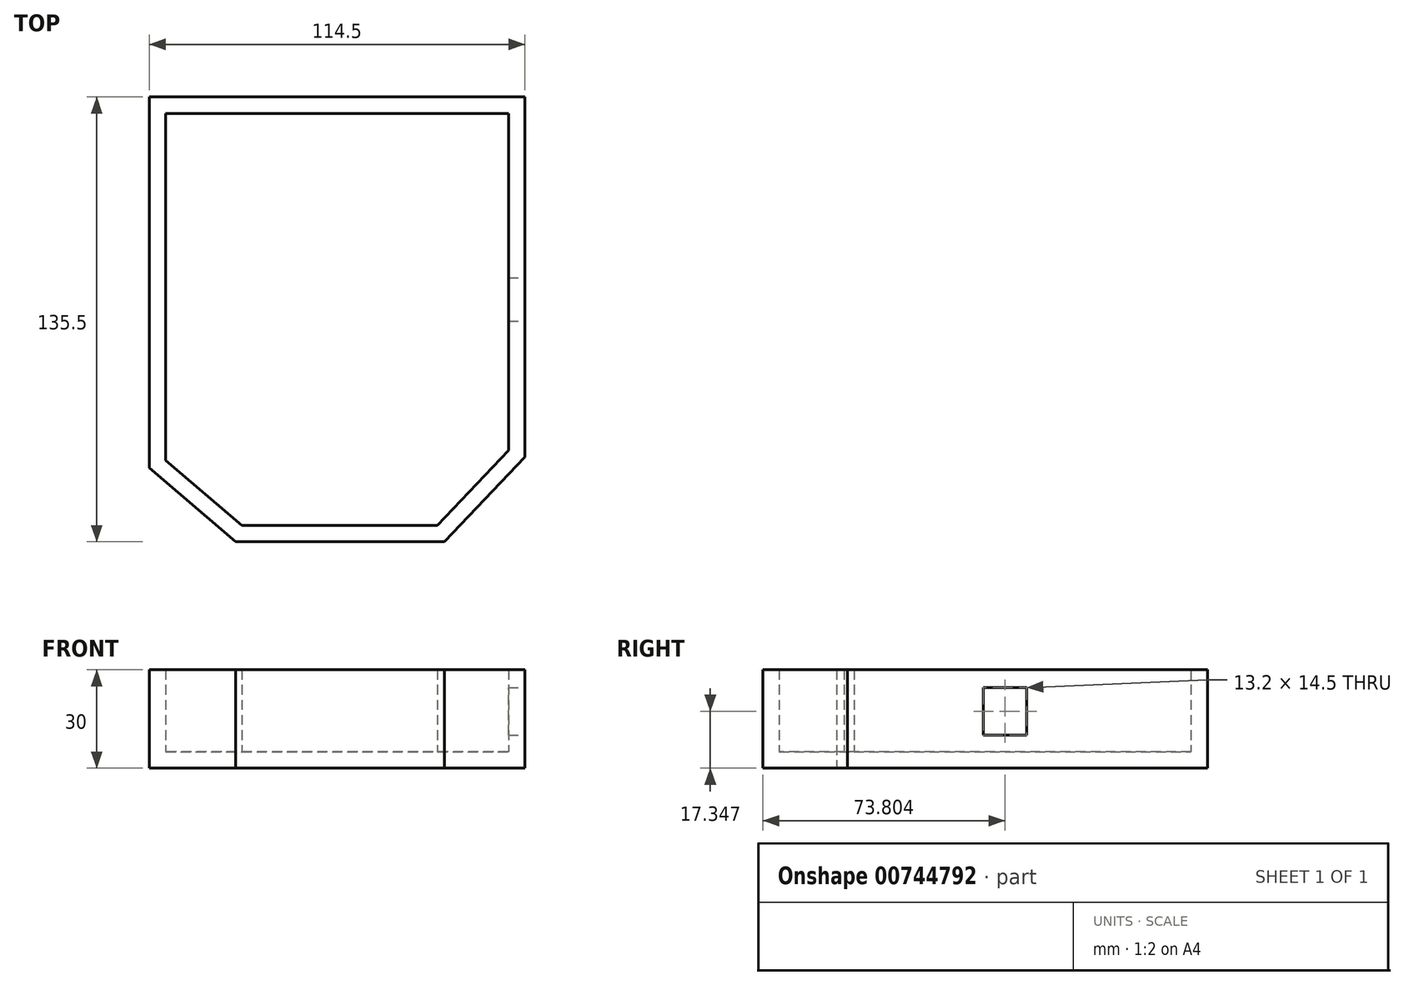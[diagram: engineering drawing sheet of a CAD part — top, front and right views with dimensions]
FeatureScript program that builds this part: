
annotation { "Feature Type Name" : "Feature", "Feature Type Description" : "" }
export const myFeature = defineFeature(function(context is Context, id is Id, definition is map)
    precondition{}
    {
        {
            var Q0;
            Q0=qCreatedBy(makeId("Top.planeOp"),FACE);
            var sketch = newSketch(context, id + "F0", { "sketchPlane" : qUnion([Q0])});
            skLineSegment(sketch, "E0.bottom", {"start": v(-53, 54.87) * mm, "end": v(61.5, 54.87) * mm});
            skLineSegment(sketch, "E0.top", {"start": v(-28.5, -80.63) * mm, "end": v(37, -80.63) * mm});
            skLineSegment(sketch, "E0.left", {"start": v(-53, 54.87) * mm, "end": v(-53, -58.13) * mm});
            skLineSegment(sketch, "E0.right", {"start": v(61.5, 54.87) * mm, "end": v(61.5, -54.87) * mm});
            skLineSegment(sketch, "E1", {"start": v(-53, -58.13) * mm, "end": v(-26.67, -80.63) * mm});
            skLineSegment(sketch, "E2", {"start": v(-28.5, -80.63) * mm, "end": v(-26.67, -80.63) * mm});
            skLineSegment(sketch, "E3", {"start": v(37, -80.63) * mm, "end": v(61.5, -54.87) * mm});
            skPoint(sketch, "E4.orphan", {"position": v(-53, -80.63) * mm});
            skPoint(sketch, "E5.orphan", {"position": v(61.5, -80.63) * mm});
            skPoint(sketch, "E6.end.orphan", {"position": v(63.33, -58.13) * mm});
            skSolve(sketch);
        }
        {
            var Q0;
            Q0 = qSketchRegion(id + "F0", true);
            extrude(context, id + "F1", {"entities" : qUnion([Q0]), "depth" : 5 * mm, "offsetDistance" : 25 * mm});
        }
        {
            var Q0;
            Q0=makeQuery(id+"F1.opExtrude","CAP_FACE",FACE,{"disambiguationData":[OSD([sQuery(id+"F0.wireOp",EDGE,"E0.bottom"),sQuery(id+"F0.wireOp",EDGE,"E0.top"),sQuery(id+"F0.wireOp",EDGE,"E0.left"),sQuery(id+"F0.wireOp",EDGE,"E0.right"),sQuery(id+"F0.wireOp",EDGE,"E1"),sQuery(id+"F0.wireOp",EDGE,"E3")])],"isStart":false});
            var sketch = newSketch(context, id + "F2", { "sketchPlane" : qUnion([Q0])});
            skLineSegment(sketch, "E7.0", {"start": v(-48, 49.87) * mm, "end": v(-48, -55.83) * mm});
            skLineSegment(sketch, "E7.1", {"start": v(-24.83, -75.63) * mm, "end": v(34.86, -75.63) * mm});
            skLineSegment(sketch, "E7.2", {"start": v(34.86, -75.63) * mm, "end": v(56.5, -52.87) * mm});
            skLineSegment(sketch, "E7.3", {"start": v(-48, -55.83) * mm, "end": v(-24.83, -75.63) * mm});
            skLineSegment(sketch, "E7.4", {"start": v(56.5, -52.87) * mm, "end": v(56.5, 49.87) * mm});
            skLineSegment(sketch, "E7.5", {"start": v(56.5, 49.87) * mm, "end": v(-48, 49.87) * mm});
            skSolve(sketch);
        }
        {
            var Q0;
            Q0=makeQuery(id+"F2.imprint","IMPRINT",FACE,{"disambiguationData":[TD([[makeQuery(id+"F2.imprint","IMPRINT",EDGE,{"derivedFrom":sQuery(id+"F2.wireOp",EDGE,"E7.0")}),-1.0]])]});
            extrude(context, id + "F3", {"entities" : qUnion([Q0]), "operationType" : NewBodyOperationType.ADD, "depth" : 25 * mm, "offsetDistance" : 25 * mm});
        }
        {
            var Q0;
            {var subQ0=sQuery(id+"F0.wireOp",EDGE,"E0.right");Q0=makeQuery(id+"F3.boolean.opBoolean","MERGE",FACE,{"derivedFrom":[makeQuery(id+"F1.opExtrude","SWEPT_FACE",FACE,{"disambiguationData":[OSD([subQ0])]}),makeQuery(id+"F3.opExtrude","SWEPT_FACE",FACE,{"disambiguationData":[OSD([subQ0])]})]});}
            var sketch = newSketch(context, id + "F4", { "sketchPlane" : qUnion([Q0])});
            skLineSegment(sketch, "E8.bottom", {"start": v(10.11, 12.6) * mm, "end": v(52.11, 12.6) * mm});
            skLineSegment(sketch, "E8.top", {"start": v(10.11, 5) * mm, "end": v(52.11, 5) * mm});
            skLineSegment(sketch, "E8.left", {"start": v(10.11, 12.6) * mm, "end": v(10.11, 5) * mm});
            skLineSegment(sketch, "E8.right", {"start": v(52.11, 12.6) * mm, "end": v(52.11, 5) * mm});
            skSolve(sketch);
        }
        {
            var Q0;
            {var subQ0=sQuery(id+"F0.wireOp",EDGE,"E0.right");Q0=makeQuery(id+"F3.boolean.opBoolean","MERGE",FACE,{"derivedFrom":[makeQuery(id+"F1.opExtrude","SWEPT_FACE",FACE,{"disambiguationData":[OSD([subQ0])]}),makeQuery(id+"F3.opExtrude","SWEPT_FACE",FACE,{"disambiguationData":[OSD([subQ0])]})]});}
            var sketch = newSketch(context, id + "F5", { "sketchPlane" : qUnion([Q0])});
            skLineSegment(sketch, "E9.bottom", {"start": v(-13.43, 24.6) * mm, "end": v(-0.23, 24.6) * mm});
            skLineSegment(sketch, "E9.top", {"start": v(-13.43, 10.1) * mm, "end": v(-0.23, 10.1) * mm});
            skLineSegment(sketch, "E9.left", {"start": v(-13.43, 24.6) * mm, "end": v(-13.43, 10.1) * mm});
            skLineSegment(sketch, "E9.right", {"start": v(-0.23, 24.6) * mm, "end": v(-0.23, 10.1) * mm});
            skSolve(sketch);
        }
        {
            var Q0;
            Q0=makeQuery(id+"F5.imprint","IMPRINT",FACE,{"disambiguationData":[TD([[makeQuery(id+"F5.imprint","IMPRINT",EDGE,{"derivedFrom":sQuery(id+"F5.wireOp",EDGE,"E9.bottom")}),-1.0]])]});
            extrude(context, id + "F6", {"entities" : qUnion([Q0]), "operationType" : NewBodyOperationType.REMOVE, "oppositeDirection" : true, "depth" : 25 * mm, "offsetDistance" : 25 * mm});
        }
    });
